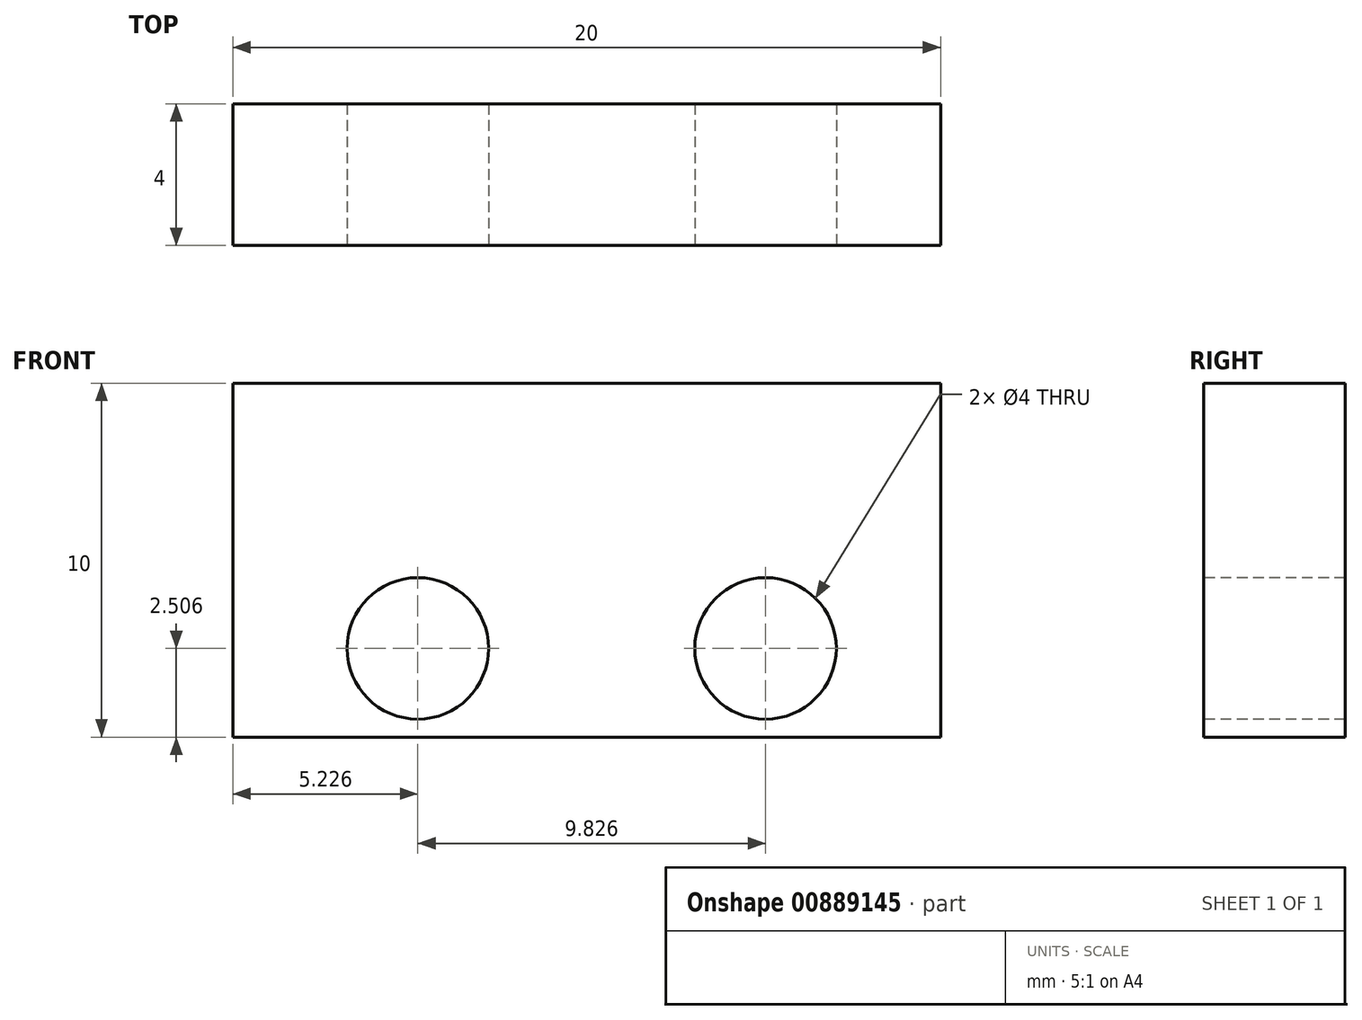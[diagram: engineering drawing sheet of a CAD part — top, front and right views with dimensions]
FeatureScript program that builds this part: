
annotation { "Feature Type Name" : "Feature", "Feature Type Description" : "" }
export const myFeature = defineFeature(function(context is Context, id is Id, definition is map)
    precondition{}
    {
        {
            var Q0;
            Q0=qCreatedBy(makeId("Front.planeOp"),FACE);
            var sketch = newSketch(context, id + "F0", { "sketchPlane" : qUnion([Q0])});
            skLineSegment(sketch, "E0.bottom", {"start": v(-10, -5) * mm, "end": v(10, -5) * mm});
            skLineSegment(sketch, "E0.top", {"start": v(-10, 5) * mm, "end": v(10, 5) * mm});
            skLineSegment(sketch, "E0.left", {"start": v(-10, -5) * mm, "end": v(-10, 5) * mm});
            skLineSegment(sketch, "E0.right", {"start": v(10, -5) * mm, "end": v(10, 5) * mm});
            skPoint(sketch, "E0.middle", {"position": v(0, 0) * mm});
            skLineSegment(sketch, "E1", {"start": v(0, -5) * mm, "end": v(0, -3.27) * mm});
            skLineSegment(sketch, "E2", {"start": v(10, -3.27) * mm, "end": v(7.17, -3.27) * mm});
            skLineSegment(sketch, "E3", {"start": v(-10, -3.27) * mm, "end": v(-7.83, -3.27) * mm});
            skPoint(sketch, "E4", {"position": v(-7.83, -3.27) * mm});
            skPoint(sketch, "E5", {"position": v(7.17, -3.27) * mm});
            skSolve(sketch);
        }
        {
            var Q0;
            {var subQ4=sQuery(id+"F0.wireOp",EDGE,"E0.top");Q0=makeQuery(id+"F0.imprint","IMPRINT",FACE,{"disambiguationData":[TD([[makeQuery(id+"F0.imprint","IMPRINT",EDGE,{"derivedFrom":subQ4}),-1.0]])]});}
            extrude(context, id + "F1", {"entities" : qUnion([Q0]), "oppositeDirection" : true, "depth" : 4 * mm, "offsetDistance" : 25 * mm});
        }
        {
            var Q0;
            Q0=makeQuery(id+"F1.opExtrude","CAP_FACE",FACE,{"disambiguationData":[OSD([sQuery(id+"F0.wireOp",EDGE,"E0.bottom"),sQuery(id+"F0.wireOp",EDGE,"E0.top"),sQuery(id+"F0.wireOp",EDGE,"E0.left"),sQuery(id+"F0.wireOp",EDGE,"E0.right")])],"isStart":true});
            var sketch = newSketch(context, id + "F2", { "sketchPlane" : qUnion([Q0])});
            skLineSegment(sketch, "E6", {"start": v(0, -5) * mm, "end": v(0, -2.5) * mm});
            skLineSegment(sketch, "E7", {"start": v(10, -2.5) * mm, "end": v(5.05, -2.5) * mm});
            skLineSegment(sketch, "E8", {"start": v(-10, -2.5) * mm, "end": v(-4.77, -2.5) * mm});
            skPoint(sketch, "E9", {"position": v(-4.77, -2.5) * mm});
            skPoint(sketch, "E10", {"position": v(5.05, -2.5) * mm});
            skSolve(sketch);
        }
        {
            var Q0;
            Q0=sQuery(id+"F2.wireOp",VERTEX,"E9");
            var Q1;
            Q1=sQuery(id+"F2.wireOp",VERTEX,"E10");
            var Q2;
            Q2=makeQuery(id+"F1.opExtrude","SWEPT_BODY",BODY,{"disambiguationData":[OSD([sQuery(id+"F0.wireOp",EDGE,"E0.bottom"),sQuery(id+"F0.wireOp",EDGE,"E0.top"),sQuery(id+"F0.wireOp",EDGE,"E0.left"),sQuery(id+"F0.wireOp",EDGE,"E0.right")])]});
            hole(context, id + "F3", {"style" : HoleStyle.SIMPLE, "endStyle" : HoleEndStyle.BLIND, "holeDiameter" : 4 * mm, "majorDiameter" : 5 * mm, "holeDepth" : 20 * mm, "isTappedThrough" : true, "tappedDepth" : 12 * mm, "tapClearance" : 3, "startFromSketch" : true, "locations" : qUnion([Q0, Q1]), "scope" : qUnion([Q2])});
        }
    });
